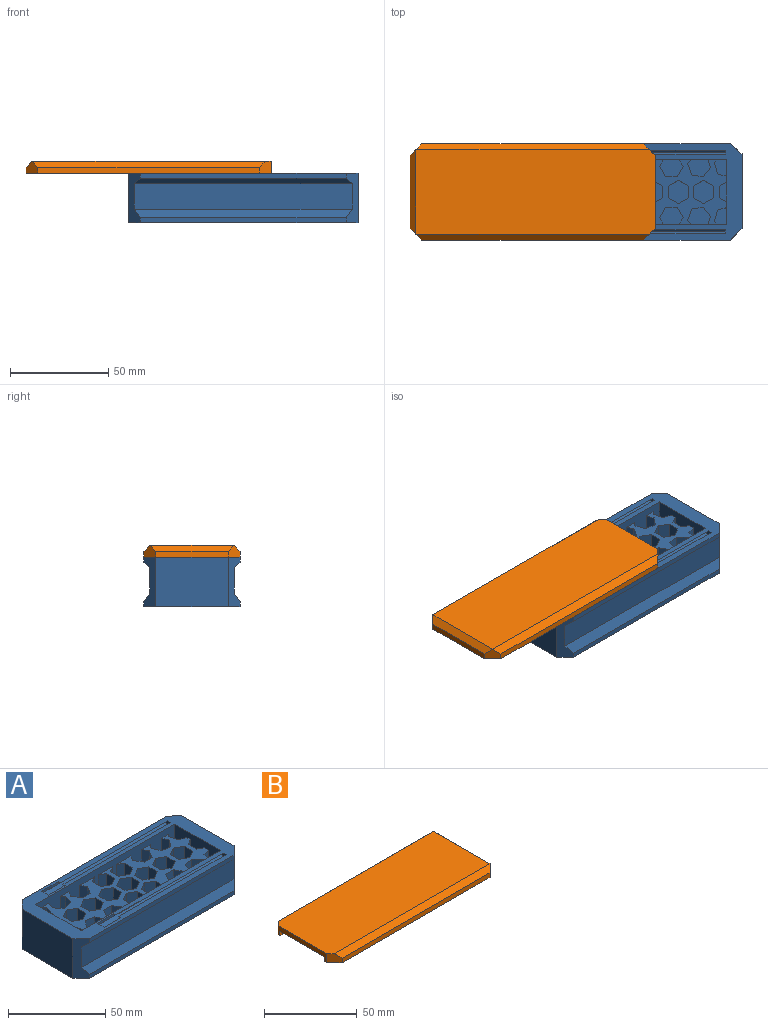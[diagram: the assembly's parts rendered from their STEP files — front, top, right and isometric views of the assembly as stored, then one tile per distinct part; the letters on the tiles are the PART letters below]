
ASSEMBLY  parts=2 mates=1
PART A: 196 faces, bbox 117x49x25 mm
  f0: plane 117x49mm, normal (0,0,1), area 1898.6mm2, adj f1,f2,f3,f4,f6,f7,f9,f11
  f1: plane 78x1.4mm, normal (0,-0.71,-0.71), area 154.4mm2, adj f0,f181,f182,f185
  f2: plane 78x1.4mm, normal (0,0.71,-0.71), area 154.4mm2, adj f0,f180,f182,f189
  f3: plane 105x2.53mm, normal (0,1,0), area 265.6mm2, adj f0,f9,f11,f171
  f4: plane 25x6mm, normal (-0.71,-0.71,0), area 141mm2, adj f0,f5,f6,f12,f18,f168,f169,f170
  f5: plane 105x2.47mm, normal (0,-1,0), area 259.7mm2, adj f4,f7,f18,f168
  f6: plane 105x2.53mm, normal (0,-1,0), area 265.6mm2, adj f0,f4,f7,f170
  f7: plane 25x6mm, normal (0.71,-0.71,0), area 141mm2, adj f0,f5,f6,f17,f18,f168,f169,f170
  f8: plane 101x33mm, normal (0,0,1), area 1439.9mm2, adj f13,f14,f15,f16,f19,f20,f21,f23
  f9: plane 25x6mm, normal (0.65,0.76,0), area 120.4mm2, adj f0,f3,f10,f17,f18,f171,f172,f173
  f10: plane 105x2.47mm, normal (0,1,0), area 259.7mm2, adj f9,f11,f18,f173
  f11: plane 25x6mm, normal (-0.71,0.71,0), area 141mm2, adj f0,f3,f10,f12,f18,f171,f172,f173
  f12: plane 37x25mm, normal (-1,0,0), area 925mm2, adj f0,f4,f11,f18
  f13: plane 33x19mm, normal (1,0,0), area 540.8mm2, adj f0,f8,f14,f16,f19,f22,f107,f108
  f14: plane 101x19mm, normal (0,-1,0), area 1114.2mm2, adj f0,f8,f13,f15,f21,f22,f49,f53
  f15: plane 33x19mm, normal (-1,0,0), area 540.8mm2, adj f0,f8,f14,f16,f57,f58,f59,f60
  f16: plane 101x19mm, normal (0,1,0), area 1114.2mm2, adj f0,f8,f13,f15,f30,f34,f35,f36
  f17: plane 37.86x25mm, normal (1,0,0), area 946.4mm2, adj f0,f7,f9,f18
  f18: plane 117x49mm, normal (0,0,-1), area 5663.6mm2, adj f4,f5,f7,f9,f10,f11,f12,f17
  f19: plane 15x4.51mm, normal (-0.26,0.97,0), area 70.1mm2, adj f8,f13,f20,f22
  f20: plane 15x5.8mm, normal (-0.97,0.26,0), area 90mm2, adj f8,f19,f21,f22
  f21: plane 15x1.49mm, normal (-0.71,-0.71,0), area 31.6mm2, adj f8,f14,f20,f22
  f22: plane 8.49x6.07mm, normal (0,0,1), area 41.3mm2, adj f13,f14,f19,f20,f21
  f23: plane 15x6mm, normal (1,0,0), area 90mm2, adj f8,f24,f28,f29
  f24: plane 15x5.2mm, normal (0.5,0.87,0), area 90mm2, adj f8,f23,f25,f29
  f25: plane 15x5.2mm, normal (-0.5,0.87,0), area 90mm2, adj f8,f24,f26,f29
  f26: plane 15x6mm, normal (-1,0,0), area 90mm2, adj f8,f25,f27,f29
  f27: plane 15x5.2mm, normal (-0.5,-0.87,0), area 90mm2, adj f8,f26,f28,f29
  f28: plane 15x5.2mm, normal (0.5,-0.87,0), area 90mm2, adj f8,f23,f27,f29
  f29: plane 12x10.39mm, normal (0,0,1), area 93.5mm2, adj f23,f24,f25,f26,f27,f28
  f30: plane 15x4.2mm, normal (-0.94,0.34,0), area 67.1mm2, adj f8,f16,f31,f35
  f31: plane 15x4.6mm, normal (-0.77,-0.64,0), area 90mm2, adj f8,f30,f32,f35
  f32: plane 15x5.91mm, normal (0.17,-0.98,0), area 90mm2, adj f8,f31,f33,f35
  f33: plane 15x5.64mm, normal (0.94,-0.34,0), area 90mm2, adj f8,f32,f34,f35
  f34: plane 15x2.12mm, normal (0.77,0.64,0), area 41.5mm2, adj f8,f16,f33,f35
  f35: plane 11.82x8.8mm, normal (0,0,1), area 79mm2, adj f16,f30,f31,f32,f33,f34
  f36: plane 15x3.5mm, normal (0.87,0.5,0), area 60.6mm2, adj f8,f16,f40,f41
  f37: plane 15x3.5mm, normal (-0.87,0.5,0), area 60.6mm2, adj f8,f16,f38,f41
  f38: plane 15x5.2mm, normal (-0.87,-0.5,0), area 90mm2, adj f8,f37,f39,f41
  f39: plane 15x6mm, normal (0,-1,0), area 90mm2, adj f8,f38,f40,f41
  f40: plane 15x5.2mm, normal (0.87,-0.5,0), area 90mm2, adj f8,f36,f39,f41
  f41: plane 12x8.7mm, normal (0,0,1), area 81.7mm2, adj f16,f36,f37,f38,f39,f40
  f42: plane 15x6mm, normal (1,0,0), area 90mm2, adj f8,f43,f47,f48
  f43: plane 15x5.2mm, normal (0.5,0.87,0), area 90mm2, adj f8,f42,f44,f48
  f44: plane 15x5.2mm, normal (-0.5,0.87,0), area 90mm2, adj f8,f43,f45,f48
  f45: plane 15x6mm, normal (-1,0,0), area 90mm2, adj f8,f44,f46,f48
  f46: plane 15x5.2mm, normal (-0.5,-0.87,0), area 90mm2, adj f8,f45,f47,f48
  f47: plane 15x5.2mm, normal (0.5,-0.87,0), area 90mm2, adj f8,f42,f46,f48
  f48: plane 12x10.39mm, normal (0,0,1), area 93.5mm2, adj f42,f43,f44,f45,f46,f47
  f49: plane 15x2.12mm, normal (0.77,-0.64,0), area 41.5mm2, adj f8,f14,f50,f54
  f50: plane 15x5.64mm, normal (0.94,0.34,0), area 90mm2, adj f8,f49,f51,f54
  f51: plane 15x5.91mm, normal (0.17,0.98,0), area 90mm2, adj f8,f50,f52,f54
  f52: plane 15x4.6mm, normal (-0.77,0.64,0), area 90mm2, adj f8,f51,f53,f54
  f53: plane 15x4.2mm, normal (-0.94,-0.34,0), area 67.1mm2, adj f8,f14,f52,f54
  f54: plane 11.82x8.8mm, normal (0,0,1), area 79mm2, adj f14,f49,f50,f51,f52,f53
  f55: plane 15x1.49mm, normal (0.71,-0.71,0), area 31.6mm2, adj f8,f14,f56,f58
  f56: plane 15x5.8mm, normal (0.97,0.26,0), area 90mm2, adj f8,f55,f57,f58
  f57: plane 15x4.51mm, normal (0.26,0.97,0), area 70.1mm2, adj f8,f15,f56,f58
  f58: plane 8.49x6.07mm, normal (0,0,1), area 41.3mm2, adj f14,f15,f55,f56,f57
  f59: plane 15x3.7mm, normal (0.5,0.87,0), area 64mm2, adj f8,f15,f61,f62
  f60: plane 15x3.7mm, normal (0.5,-0.87,0), area 64mm2, adj f8,f15,f61,f62
  f61: plane 15x6mm, normal (1,0,0), area 90mm2, adj f8,f59,f60,f62
  f62: plane 10.27x3.7mm, normal (0,0,1), area 30.1mm2, adj f15,f59,f60,f61
  f63: plane 15x4.51mm, normal (0.26,-0.97,0), area 70.1mm2, adj f8,f15,f64,f66
  f64: plane 15x5.8mm, normal (0.97,-0.26,0), area 90mm2, adj f8,f63,f65,f66
  f65: plane 15x1.49mm, normal (0.71,0.71,0), area 31.6mm2, adj f8,f16,f64,f66
  f66: plane 8.49x6.07mm, normal (0,0,1), area 41.3mm2, adj f15,f16,f63,f64,f65
  f67: plane 15x3.5mm, normal (-0.87,0.5,0), area 60.6mm2, adj f8,f16,f68,f72
  f68: plane 15x5.2mm, normal (-0.87,-0.5,0), area 90mm2, adj f8,f67,f69,f72
  f69: plane 15x6mm, normal (0,-1,0), area 90mm2, adj f8,f68,f70,f72
  f70: plane 15x5.2mm, normal (0.87,-0.5,0), area 90mm2, adj f8,f69,f71,f72
  f71: plane 15x3.5mm, normal (0.87,0.5,0), area 60.6mm2, adj f8,f16,f70,f72
  f72: plane 12x8.7mm, normal (0,0,1), area 81.7mm2, adj f16,f67,f68,f69,f70,f71
  f73: plane 15x6mm, normal (-1,0,0), area 90mm2, adj f8,f74,f78,f79
  f74: plane 15x5.2mm, normal (-0.5,-0.87,0), area 90mm2, adj f8,f73,f75,f79
  f75: plane 15x5.2mm, normal (0.5,-0.87,0), area 90mm2, adj f8,f74,f76,f79
  f76: plane 15x6mm, normal (1,0,0), area 90mm2, adj f8,f75,f77,f79
  f77: plane 15x5.2mm, normal (0.5,0.87,0), area 90mm2, adj f8,f76,f78,f79
  f78: plane 15x5.2mm, normal (-0.5,0.87,0), area 90mm2, adj f8,f73,f77,f79
  f79: plane 12x10.39mm, normal (0,0,1), area 93.5mm2, adj f73,f74,f75,f76,f77,f78
  f80: plane 15x3.5mm, normal (-0.87,-0.5,0), area 60.6mm2, adj f8,f14,f84,f85
  f81: plane 15x3.5mm, normal (0.87,-0.5,0), area 60.6mm2, adj f8,f14,f82,f85
  f82: plane 15x5.2mm, normal (0.87,0.5,0), area 90mm2, adj f8,f81,f83,f85
  f83: plane 15x6mm, normal (0,1,0), area 90mm2, adj f8,f82,f84,f85
  f84: plane 15x5.2mm, normal (-0.87,0.5,0), area 90mm2, adj f8,f80,f83,f85
  f85: plane 12x8.7mm, normal (0,0,1), area 81.7mm2, adj f14,f80,f81,f82,f83,f84
  f86: plane 15x4.2mm, normal (0.94,-0.34,0), area 67.1mm2, adj f8,f14,f87,f91
  f87: plane 15x4.6mm, normal (0.77,0.64,0), area 90mm2, adj f8,f86,f88,f91
  f88: plane 15x5.91mm, normal (-0.17,0.98,0), area 90mm2, adj f8,f87,f89,f91
  f89: plane 15x5.64mm, normal (-0.94,0.34,0), area 90mm2, adj f8,f88,f90,f91
  f90: plane 15x2.12mm, normal (-0.77,-0.64,0), area 41.5mm2, adj f8,f14,f89,f91
  f91: plane 11.82x8.8mm, normal (0,0,1), area 79mm2, adj f14,f86,f87,f88,f89,f90
  f92: plane 15x6mm, normal (-1,0,0), area 90mm2, adj f8,f93,f97,f98
  f93: plane 15x5.2mm, normal (-0.5,-0.87,0), area 90mm2, adj f8,f92,f94,f98
  f94: plane 15x5.2mm, normal (0.5,-0.87,0), area 90mm2, adj f8,f93,f95,f98
  f95: plane 15x6mm, normal (1,0,0), area 90mm2, adj f8,f94,f96,f98
  f96: plane 15x5.2mm, normal (0.5,0.87,0), area 90mm2, adj f8,f95,f97,f98
  f97: plane 15x5.2mm, normal (-0.5,0.87,0), area 90mm2, adj f8,f92,f96,f98
  f98: plane 12x10.39mm, normal (0,0,1), area 93.5mm2, adj f92,f93,f94,f95,f96,f97
  f99: plane 15x2.12mm, normal (-0.77,0.64,0), area 41.5mm2, adj f8,f16,f100,f104
  f100: plane 15x5.64mm, normal (-0.94,-0.34,0), area 90mm2, adj f8,f99,f101,f104
  f101: plane 15x5.91mm, normal (-0.17,-0.98,0), area 90mm2, adj f8,f100,f102,f104
  f102: plane 15x4.6mm, normal (0.77,-0.64,0), area 90mm2, adj f8,f101,f103,f104
  f103: plane 15x4.2mm, normal (0.94,0.34,0), area 67.1mm2, adj f8,f16,f102,f104
  f104: plane 11.82x8.8mm, normal (0,0,1), area 79mm2, adj f16,f99,f100,f101,f102,f103
  f105: plane 15x1.49mm, normal (-0.71,0.71,0), area 31.6mm2, adj f8,f16,f106,f108
  f106: plane 15x5.8mm, normal (-0.97,-0.26,0), area 90mm2, adj f8,f105,f107,f108
  f107: plane 15x4.51mm, normal (-0.26,-0.97,0), area 70.1mm2, adj f8,f13,f106,f108
  f108: plane 8.49x6.07mm, normal (0,0,1), area 41.3mm2, adj f13,f16,f105,f106,f107
  f109: plane 15x3.7mm, normal (-0.5,0.87,0), area 64mm2, adj f8,f13,f110,f112
  f110: plane 15x6mm, normal (-1,0,0), area 90mm2, adj f8,f109,f111,f112
  f111: plane 15x3.7mm, normal (-0.5,-0.87,0), area 64mm2, adj f8,f13,f110,f112
  f112: plane 10.27x3.7mm, normal (0,0,1), area 30.1mm2, adj f13,f109,f110,f111
  f113: plane 15x3.88mm, normal (-0.5,0.87,0), area 67.3mm2, adj f8,f16,f114,f119
  f114: plane 15x6mm, normal (-1,0,0), area 90mm2, adj f8,f113,f115,f119
  f115: plane 15x5.2mm, normal (-0.5,-0.87,0), area 90mm2, adj f8,f114,f116,f119
  f116: plane 15x5.2mm, normal (0.5,-0.87,0), area 90mm2, adj f8,f115,f117,f119
  f117: plane 15x6mm, normal (1,0,0), area 90mm2, adj f8,f116,f118,f119
  f118: plane 15x3.88mm, normal (0.5,0.87,0), area 67.3mm2, adj f8,f16,f117,f119
  f119: plane 11.24x10.39mm, normal (0,0,1), area 92.5mm2, adj f16,f113,f114,f115,f116,f117,f118
  f120: plane 15x3.88mm, normal (0.5,0.87,0), area 67.3mm2, adj f8,f16,f125,f126
  f121: plane 15x3.88mm, normal (-0.5,0.87,0), area 67.3mm2, adj f8,f16,f122,f126
  f122: plane 15x6mm, normal (-1,0,0), area 90mm2, adj f8,f121,f123,f126
  f123: plane 15x5.2mm, normal (-0.5,-0.87,0), area 90mm2, adj f8,f122,f124,f126
  f124: plane 15x5.2mm, normal (0.5,-0.87,0), area 90mm2, adj f8,f123,f125,f126
  f125: plane 15x6mm, normal (1,0,0), area 90mm2, adj f8,f120,f124,f126
  f126: plane 11.24x10.39mm, normal (0,0,1), area 92.5mm2, adj f16,f120,f121,f122,f123,f124,f125
  f127: plane 15x6mm, normal (1,0,0), area 90mm2, adj f8,f128,f132,f133
  f128: plane 15x5.2mm, normal (0.5,0.87,0), area 90mm2, adj f8,f127,f129,f133
  f129: plane 15x5.2mm, normal (-0.5,0.87,0), area 90mm2, adj f8,f128,f130,f133
  f130: plane 15x6mm, normal (-1,0,0), area 90mm2, adj f8,f129,f131,f133
  f131: plane 15x5.2mm, normal (-0.5,-0.87,0), area 90mm2, adj f8,f130,f132,f133
  f132: plane 15x5.2mm, normal (0.5,-0.87,0), area 90mm2, adj f8,f127,f131,f133
  f133: plane 12x10.39mm, normal (0,0,1), area 93.5mm2, adj f127,f128,f129,f130,f131,f132
  f134: plane 15x3.5mm, normal (0.87,-0.5,0), area 60.6mm2, adj f8,f14,f135,f139
  f135: plane 15x5.2mm, normal (0.87,0.5,0), area 90mm2, adj f8,f134,f136,f139
  f136: plane 15x6mm, normal (0,1,0), area 90mm2, adj f8,f135,f137,f139
  f137: plane 15x5.2mm, normal (-0.87,0.5,0), area 90mm2, adj f8,f136,f138,f139
  f138: plane 15x3.5mm, normal (-0.87,-0.5,0), area 60.6mm2, adj f8,f14,f137,f139
  f139: plane 12x8.7mm, normal (0,0,1), area 81.7mm2, adj f14,f134,f135,f136,f137,f138
  f140: plane 15x3.88mm, normal (-0.5,-0.87,0), area 67.3mm2, adj f8,f14,f145,f146
  f141: plane 15x3.88mm, normal (0.5,-0.87,0), area 67.3mm2, adj f8,f14,f142,f146
  f142: plane 15x6mm, normal (1,0,0), area 90mm2, adj f8,f141,f143,f146
  f143: plane 15x5.2mm, normal (0.5,0.87,0), area 90mm2, adj f8,f142,f144,f146
  f144: plane 15x5.2mm, normal (-0.5,0.87,0), area 90mm2, adj f8,f143,f145,f146
  f145: plane 15x6mm, normal (-1,0,0), area 90mm2, adj f8,f140,f144,f146
  f146: plane 11.24x10.39mm, normal (0,0,1), area 92.5mm2, adj f14,f140,f141,f142,f143,f144,f145
  f147: plane 15x5.2mm, normal (-0.5,-0.87,0), area 90mm2, adj f8,f148,f152,f153
  f148: plane 15x5.2mm, normal (0.5,-0.87,0), area 90mm2, adj f8,f147,f149,f153
  f149: plane 15x6mm, normal (1,0,0), area 90mm2, adj f8,f148,f150,f153
  f150: plane 15x5.2mm, normal (0.5,0.87,0), area 90mm2, adj f8,f149,f151,f153
  f151: plane 15x5.2mm, normal (-0.5,0.87,0), area 90mm2, adj f8,f150,f152,f153
  f152: plane 15x6mm, normal (-1,0,0), area 90mm2, adj f8,f147,f151,f153
  f153: plane 12x10.39mm, normal (0,0,1), area 93.5mm2, adj f147,f148,f149,f150,f151,f152
  f154: plane 15x5.2mm, normal (-0.5,-0.87,0), area 90mm2, adj f8,f155,f159,f160
  f155: plane 15x5.2mm, normal (0.5,-0.87,0), area 90mm2, adj f8,f154,f156,f160
  f156: plane 15x6mm, normal (1,0,0), area 90mm2, adj f8,f155,f157,f160
  f157: plane 15x5.2mm, normal (0.5,0.87,0), area 90mm2, adj f8,f156,f158,f160
  f158: plane 15x5.2mm, normal (-0.5,0.87,0), area 90mm2, adj f8,f157,f159,f160
  f159: plane 15x6mm, normal (-1,0,0), area 90mm2, adj f8,f154,f158,f160
  f160: plane 12x10.39mm, normal (0,0,1), area 93.5mm2, adj f154,f155,f156,f157,f158,f159
  f161: plane 15x3.88mm, normal (0.5,-0.87,0), area 67.3mm2, adj f8,f14,f162,f167
  f162: plane 15x6mm, normal (1,0,0), area 90mm2, adj f8,f161,f163,f167
  f163: plane 15x5.2mm, normal (0.5,0.87,0), area 90mm2, adj f8,f162,f164,f167
  f164: plane 15x5.2mm, normal (-0.5,0.87,0), area 90mm2, adj f8,f163,f165,f167
  f165: plane 15x6mm, normal (-1,0,0), area 90mm2, adj f8,f164,f166,f167
  f166: plane 15x3.88mm, normal (-0.5,-0.87,0), area 67.3mm2, adj f8,f14,f165,f167
  f167: plane 11.24x10.39mm, normal (0,0,1), area 92.5mm2, adj f14,f161,f162,f163,f164,f165,f166
  f168: plane 111.11x4.39mm, normal (0,-0.82,0.57), area 578mm2, adj f4,f5,f7,f169
  f169: plane 111.11x12.91mm, normal (0,-1,0), area 1434.7mm2, adj f4,f7,f168,f170
  f170: plane 111.11x3.06mm, normal (0,-0.66,-0.75), area 440.1mm2, adj f4,f6,f7,f169
  f171: plane 111.62x3.06mm, normal (0,0.66,-0.75), area 441.2mm2, adj f3,f9,f11,f172
  f172: plane 111.62x12.91mm, normal (0,1,0), area 1441.3mm2, adj f9,f11,f171,f173
  f173: plane 111.62x4.39mm, normal (0,0.82,0.57), area 579.3mm2, adj f9,f10,f11,f172
  f174: plane 78x1.4mm, normal (0,-0.71,-0.71), area 154.4mm2, adj f0,f177,f178,f191
  f175: plane 78x1.4mm, normal (0,0.71,-0.71), area 154.4mm2, adj f0,f176,f178,f195
  f176: plane 90x2.4mm, normal (0,0.71,0.71), area 305.5mm2, adj f175,f177,f178,f179,f193
  f177: plane 90x2.4mm, normal (0,-0.71,0.71), area 305.5mm2, adj f174,f176,f178,f179,f190
  f178: plane 4.8x3.8mm, normal (-1,0,0), area 10.5mm2, adj f0,f174,f175,f176,f177
  f179: plane 5x3.8mm, normal (1,0,0), area 12.8mm2, adj f0,f176,f177,f190,f192,f193,f194
  f180: plane 90x2.4mm, normal (0,0.71,0.71), area 305.5mm2, adj f2,f181,f182,f183,f187
  f181: plane 90x2.4mm, normal (0,-0.71,0.71), area 305.5mm2, adj f1,f180,f182,f183,f184
  f182: plane 4.8x3.8mm, normal (-1,0,0), area 10.5mm2, adj f0,f1,f2,f180,f181
  f183: plane 5x3.8mm, normal (1,0,0), area 12.8mm2, adj f0,f180,f181,f184,f186,f187,f188
  f184: plane 12x0.1mm, normal (0,0,1), area 1.2mm2, adj f181,f183,f185,f186
  f185: plane 1.5x1.4mm, normal (-1,0,0), area 1.1mm2, adj f0,f1,f184,f186
  f186: plane 12x1.4mm, normal (0,-1,0), area 16.8mm2, adj f0,f183,f184,f185
  f187: plane 12x0.1mm, normal (0,0,1), area 1.2mm2, adj f180,f183,f188,f189
  f188: plane 12x1.4mm, normal (0,1,0), area 16.8mm2, adj f0,f183,f187,f189
  f189: plane 1.5x1.4mm, normal (-1,0,0), area 1.1mm2, adj f0,f2,f187,f188
  f190: plane 12x0.1mm, normal (0,0,1), area 1.2mm2, adj f177,f179,f191,f192
  f191: plane 1.5x1.4mm, normal (-1,0,0), area 1.1mm2, adj f0,f174,f190,f192
  f192: plane 12x1.4mm, normal (0,-1,0), area 16.8mm2, adj f0,f179,f190,f191
  f193: plane 12x0.1mm, normal (0,0,1), area 1.2mm2, adj f176,f179,f194,f195
  f194: plane 12x1.4mm, normal (0,1,0), area 16.8mm2, adj f0,f179,f193,f195
  f195: plane 1.5x1.4mm, normal (-1,0,0), area 1.1mm2, adj f0,f175,f193,f194
PART B: 35 faces, bbox 125x49x9.7 mm
  f0: plane 125x49mm, normal (0,0,-1), area 2008.9mm2, adj f1,f2,f3,f4,f5,f6,f7,f8
  f1: plane 113x3mm, normal (0,1,0), area 339mm2, adj f0,f2,f8,f34
  f2: plane 6x6mm, normal (-0.71,0.71,0), area 44.5mm2, adj f0,f1,f3,f9,f34
  f3: plane 37x6mm, normal (-1,0,0), area 120mm2, adj f0,f2,f4,f9,f28,f29,f31
  f4: plane 6x6mm, normal (-0.71,-0.71,0), area 44.5mm2, adj f0,f3,f5,f9,f32
  f5: plane 113x3mm, normal (0,-1,0), area 339mm2, adj f0,f4,f6,f32
  f6: plane 6x6mm, normal (0.71,-0.71,0), area 38.2mm2, adj f0,f5,f7,f32,f33
  f7: plane 37x3mm, normal (1,0,0), area 111mm2, adj f0,f6,f8,f33
  f8: plane 6x6mm, normal (0.71,0.71,0), area 38.2mm2, adj f0,f1,f7,f33,f34
  f9: plane 122x43mm, normal (0,0,1), area 5237mm2, adj f2,f3,f4,f32,f33,f34
  f10: plane 4.23x3.72mm, normal (1,0,0), area 8.8mm2, adj f0,f11,f13,f14,f15,f16,f17,f18
  f11: plane 10x0.01mm, normal (0,1,-0.01), area 0.1mm2, adj f0,f10,f12,f16
  f12: plane 4.23x3.72mm, normal (-1,0,0), area 8.8mm2, adj f0,f11,f13,f14,f15,f16,f17,f18
  f13: plane 10x2.12mm, normal (0,-0.71,-0.71), area 29.9mm2, adj f10,f12,f14,f18
  f14: plane 10x2.12mm, normal (0,0.71,-0.71), area 29.9mm2, adj f10,f12,f13,f15
  f15: plane 10x1.31mm, normal (0,0.71,0.71), area 18.5mm2, adj f10,f12,f14,f16
  f16: plane 10x0.27mm, normal (0,1,0), area 2.7mm2, adj f10,f11,f12,f15
  f17: plane 10x0.28mm, normal (0,-1,0), area 2.8mm2, adj f0,f10,f12,f18
  f18: plane 10x1.32mm, normal (0,-0.71,0.71), area 18.6mm2, adj f10,f12,f13,f17
  f19: plane 4.23x3.72mm, normal (1,0,0), area 8.8mm2, adj f0,f21,f22,f23,f24,f25,f26,f27
  f20: plane 4.23x3.72mm, normal (-1,0,0), area 8.8mm2, adj f0,f21,f22,f23,f24,f25,f26,f27
  f21: plane 10x0.01mm, normal (0,-1,0.01), area 0.1mm2, adj f0,f19,f20,f22
  f22: plane 10x0.27mm, normal (0,-1,0), area 2.7mm2, adj f19,f20,f21,f23
  f23: plane 10x1.31mm, normal (0,-0.71,0.71), area 18.5mm2, adj f19,f20,f22,f24
  f24: plane 10x2.12mm, normal (0,-0.71,-0.71), area 29.9mm2, adj f19,f20,f23,f25
  f25: plane 10x2.12mm, normal (0,0.71,-0.71), area 29.9mm2, adj f19,f20,f24,f26
  f26: plane 10x1.32mm, normal (0,0.71,0.71), area 18.6mm2, adj f19,f20,f25,f27
  f27: plane 10x0.28mm, normal (0,1,0), area 2.8mm2, adj f0,f19,f20,f26
  f28: plane 118x3mm, normal (0,1,0), area 354mm2, adj f0,f3,f30,f31
  f29: plane 118x3mm, normal (0,-1,0), area 354mm2, adj f0,f3,f30,f31
  f30: plane 34x3mm, normal (-1,0,0), area 102mm2, adj f0,f28,f29,f31
  f31: plane 118x34mm, normal (0,0,-1), area 4012mm2, adj f3,f28,f29,f30
  f32: plane 119x3mm, normal (0,-0.71,0.71), area 492.1mm2, adj f4,f5,f6,f9
  f33: plane 43x3mm, normal (0.71,0,0.71), area 169.7mm2, adj f6,f7,f8,f9
  f34: plane 119x3mm, normal (0,0.71,0.71), area 492.1mm2, adj f1,f2,f8,f9
PLACE A t=(-18.61,-21.28,49.58)mm fixed
PLACE B rot(axis=(0,0,1),180deg) t=(-66.86,-21.28,74.7)mm
MATE slider B.f19 <-> A.f183  axis (-1,0,0) through (-26.86,-1.06,70.98)mm
